# Revit family: Deca_Alça de apoio Deca Hotel_2077.C
name_source: partatom
category: Plumbing Fixtures
revit_build: Autodesk Revit Architecture 2012 (Build: 20120126_0600(x64)
units: mm (PartAtom-declared; Revit-internal decimal feet)

## types (2) — shared parameters
Atendimento ao Cliente = 0800-011-7073
Barra = Deca CR10 Cromado Metal
Código = 2077.C
Description = Alça de apoio
Informações Complementares = Alça de apoio suporta até 60kg
Linha = Acessórios Deca Hotel
Louça/Metais = Metal
Manufacturer = Deca
Material = Deca_Latão Cromado e Plástico de Engenharia
Model = 2077.C
Norma = ABNT NBR 10283:2003
Produto = Alça de apoio Deca Hotel
Segmento = Médio
Variações de COR = Cromado (2077.C)
zero-valued in all types: CWFU, HWFU

## per-type parameters (varying)
| type | Assembly Code | Default Elevation | Peso Liquido (Kg) | URL |
| 2310.C.080.POL.10 |  | 0 mm  [stored 0 ft] | 0 | www.deca.com.br |
| 2077.C_Cromado CR10 | D20 | 700 mm  [stored 2.29659 ft] | 0.45 | www.deca.com.br/produtos |

note: [stored X ft] marks values corroborated as IEEE doubles in the binary element streams (Revit-internal decimal feet)

## geometry (parser evidence)
native form markers: Blend x4, Sweep x1
no freeform markers — native parametric forms only
